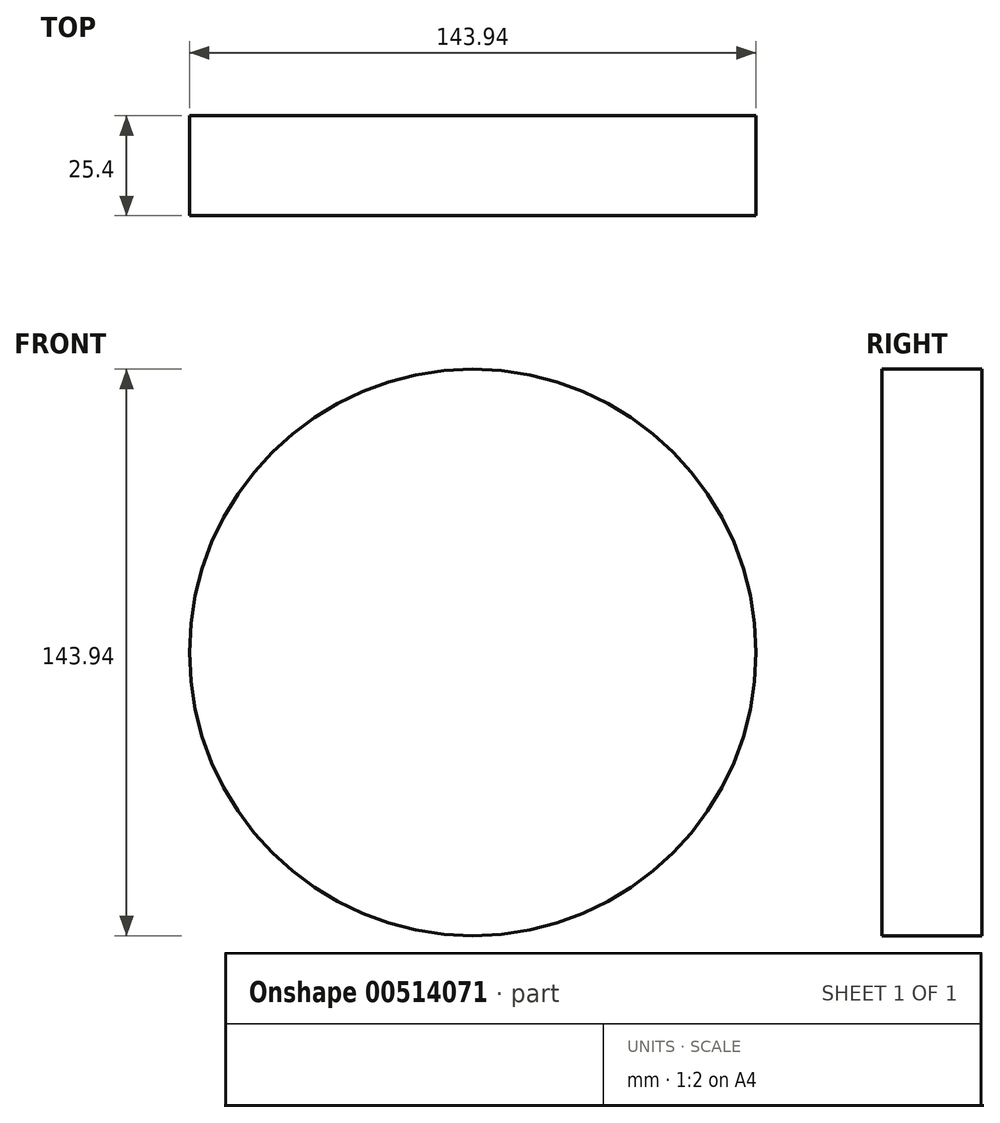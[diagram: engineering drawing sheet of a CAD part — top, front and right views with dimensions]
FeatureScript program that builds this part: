
annotation { "Feature Type Name" : "Feature", "Feature Type Description" : "" }
export const myFeature = defineFeature(function(context is Context, id is Id, definition is map)
    precondition{}
    {
        {
            var Q0;
            Q0=qCreatedBy(makeId("Front.planeOp"),FACE);
            var sketch = newSketch(context, id + "F0", { "sketchPlane" : qUnion([Q0])});
            skCircle(sketch, "E0", {"center": v(0, 0) * mm, "radius": 71.97 * mm});
            skSolve(sketch);
        }
        {
            var Q0;
            Q0 = qSketchRegion(id + "F0", true);
            extrude(context, id + "F1", {"entities" : qUnion([Q0]), "depth" : 25.4 * mm});
        }
    });
